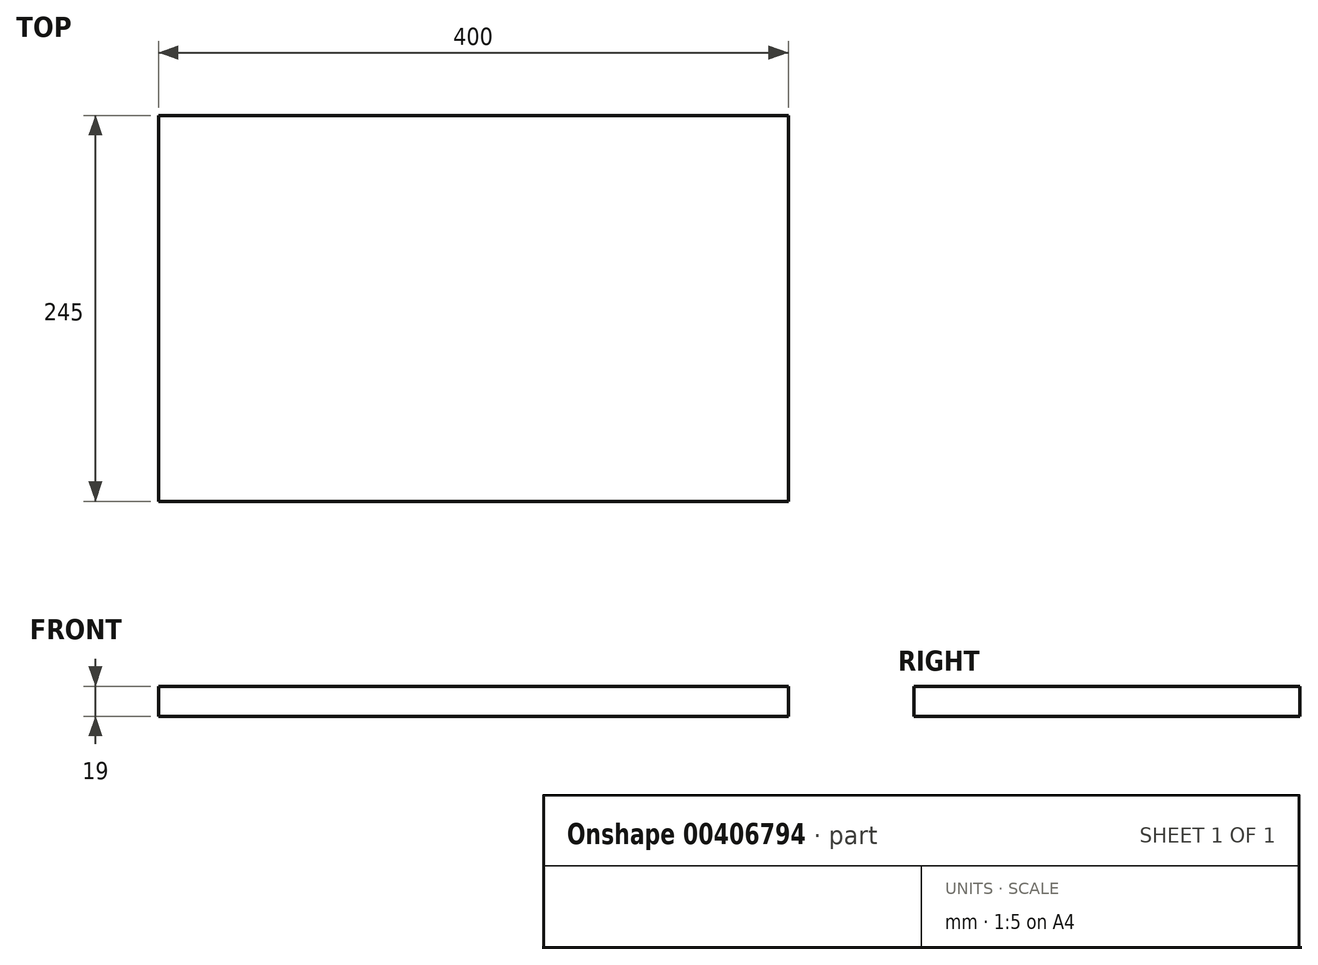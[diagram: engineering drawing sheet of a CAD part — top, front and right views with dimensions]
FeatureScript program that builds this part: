
annotation { "Feature Type Name" : "Feature", "Feature Type Description" : "" }
export const myFeature = defineFeature(function(context is Context, id is Id, definition is map)
    precondition{}
    {
        {
            var Q0;
            Q0=qCreatedBy(makeId("Top.planeOp"),FACE);
            var sketch = newSketch(context, id + "F0", { "sketchPlane" : qUnion([Q0])});
            skLineSegment(sketch, "E0.bottom", {"start": v(0, 0) * mm, "end": v(400, 0) * mm});
            skLineSegment(sketch, "E0.top", {"start": v(0, 245) * mm, "end": v(400, 245) * mm});
            skLineSegment(sketch, "E0.left", {"start": v(0, 0) * mm, "end": v(0, 245) * mm});
            skLineSegment(sketch, "E0.right", {"start": v(400, 0) * mm, "end": v(400, 245) * mm});
            skSolve(sketch);
        }
        {
            var Q0;
            Q0=makeQuery(id+"F0.imprint","IMPRINT",FACE,{"disambiguationData":[TD([[makeQuery(id+"F0.imprint","IMPRINT",EDGE,{"derivedFrom":sQuery(id+"F0.wireOp",EDGE,"E0.bottom")}),1.0]])]});
            extrude(context, id + "F1", {"entities" : qUnion([Q0]), "depth" : 19 * mm});
        }
    });
